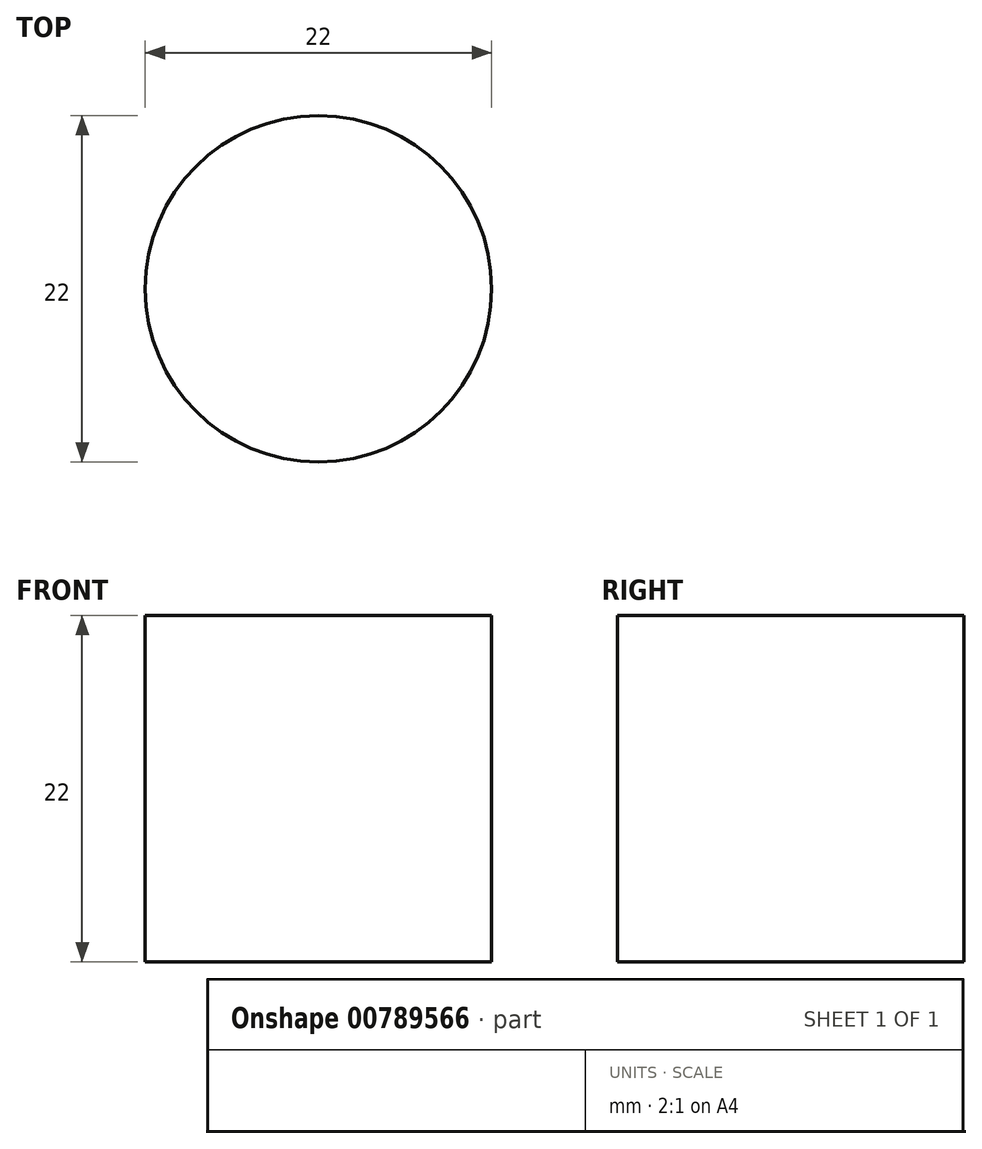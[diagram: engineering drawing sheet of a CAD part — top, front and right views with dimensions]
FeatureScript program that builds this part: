
annotation { "Feature Type Name" : "Feature", "Feature Type Description" : "" }
export const myFeature = defineFeature(function(context is Context, id is Id, definition is map)
    precondition{}
    {
        {
            var Q0;
            Q0=qCreatedBy(makeId("Top.planeOp"),FACE);
            var sketch = newSketch(context, id + "F0", { "sketchPlane" : qUnion([Q0])});
            skCircle(sketch, "E0", {"center": v(0, 0) * mm, "radius": 11 * mm});
            skSolve(sketch);
        }
        {
            var Q0;
            Q0 = qSketchRegion(id + "F0", true);
            extrude(context, id + "F1", {"entities" : qUnion([Q0]), "depth" : 22 * mm, "offsetDistance" : 25 * mm});
        }
    });
